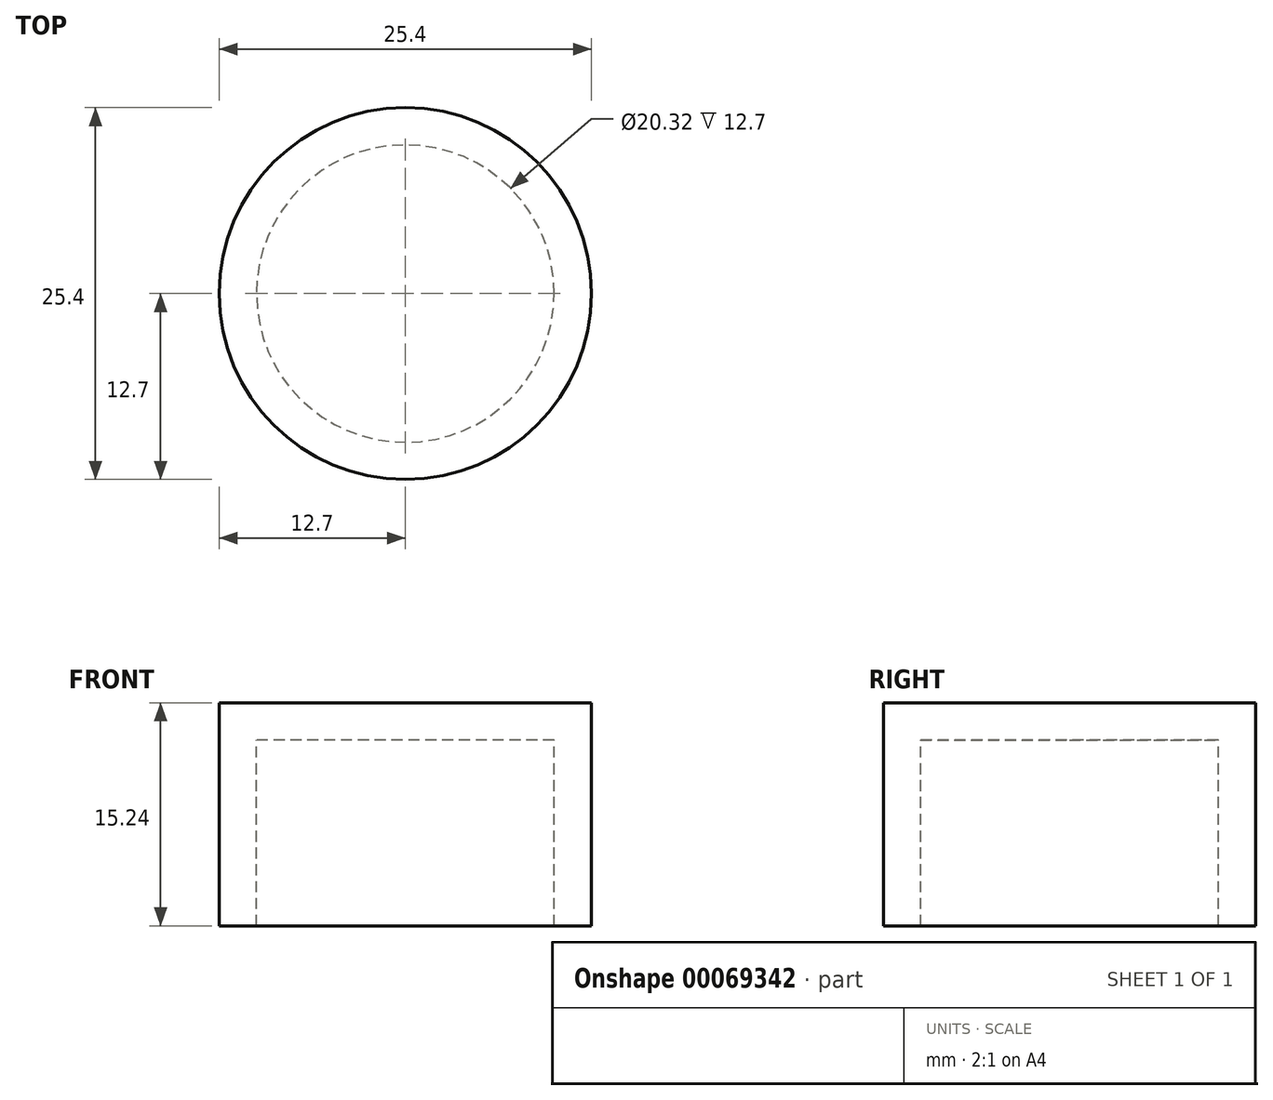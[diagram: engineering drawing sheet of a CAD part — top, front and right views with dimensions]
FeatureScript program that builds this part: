
annotation { "Feature Type Name" : "Feature", "Feature Type Description" : "" }
export const myFeature = defineFeature(function(context is Context, id is Id, definition is map)
    precondition{}
    {
        {
            var Q0;
            Q0=qCreatedBy(makeId("Top.planeOp"),FACE);
            var sketch = newSketch(context, id + "F0", { "sketchPlane" : qUnion([Q0])});
            skCircle(sketch, "E0", {"center": v(0, 0) * mm, "radius": 12.7 * mm});
            skCircle(sketch, "E1", {"center": v(0, 0) * mm, "radius": 10.16 * mm});
            skSolve(sketch);
        }
        {
            var Q0;
            Q0=makeQuery(id+"F0.imprint","IMPRINT",FACE,{"disambiguationData":[TD([[makeQuery(id+"F0.imprint","IMPRINT",EDGE,{"derivedFrom":sQuery(id+"F0.wireOp",EDGE,"E1")}),1.0]])]});
            var Q1;
            Q1=makeQuery(id+"F0.imprint","IMPRINT",FACE,{"disambiguationData":[TD([[makeQuery(id+"F0.imprint","IMPRINT",EDGE,{"derivedFrom":sQuery(id+"F0.wireOp",EDGE,"E0")}),1.0]])]});
            extrude(context, id + "F1", {"entities" : qUnion([Q0, Q1]), "depth" : 2.54 * mm});
        }
        {
            var Q0;
            Q0 = qSketchRegion(id + "F0", true);
            extrude(context, id + "F2", {"entities" : qUnion([Q0]), "operationType" : NewBodyOperationType.ADD, "oppositeDirection" : true, "depth" : 12.7 * mm});
        }
    });
